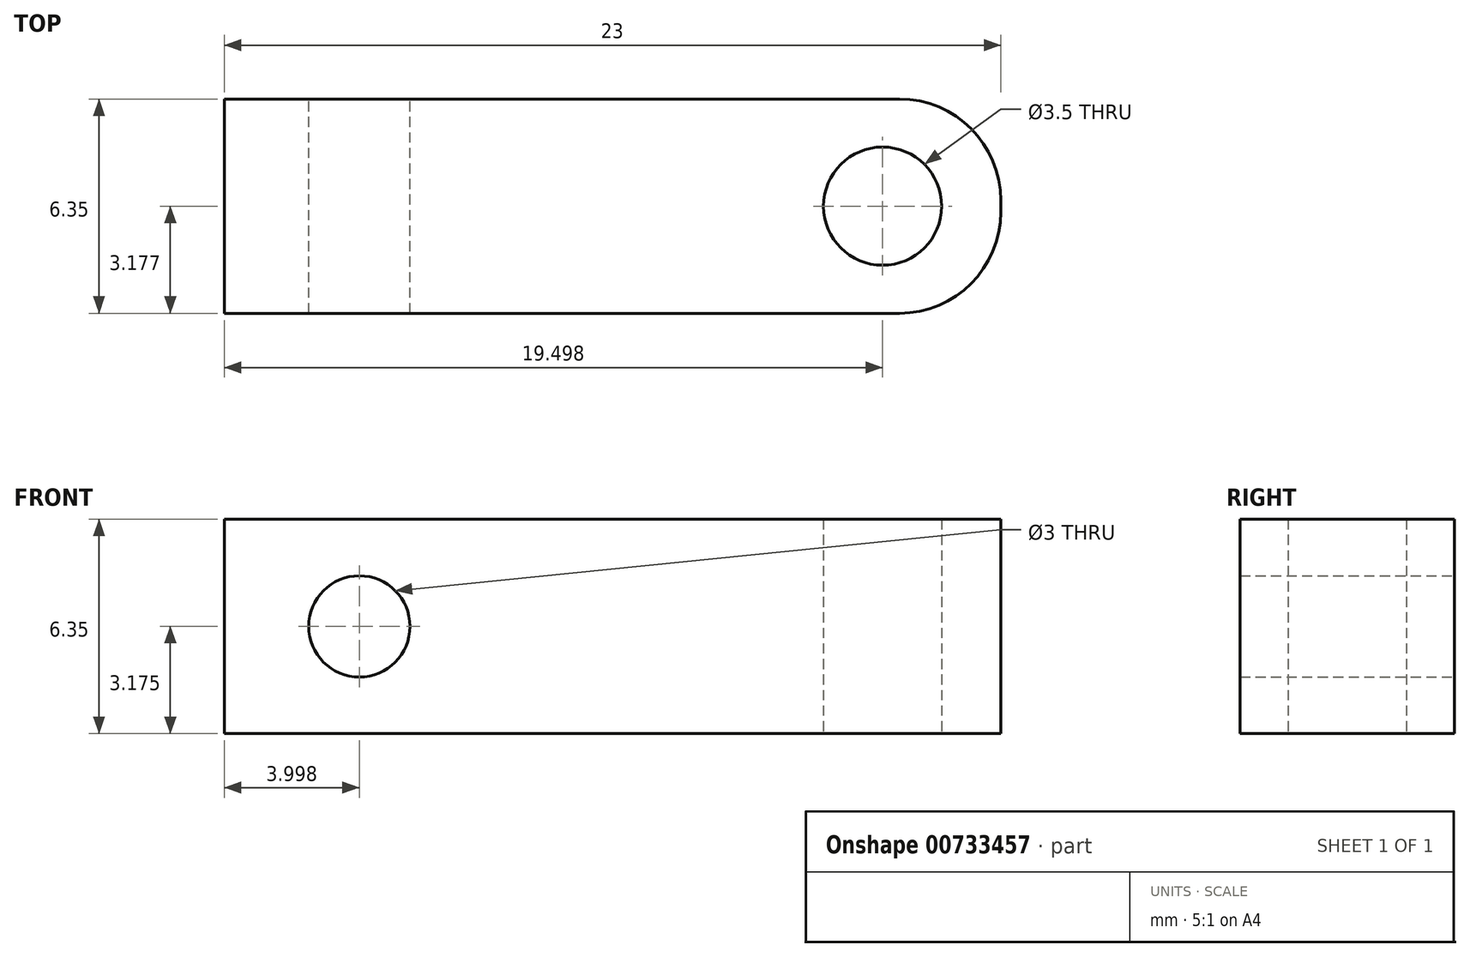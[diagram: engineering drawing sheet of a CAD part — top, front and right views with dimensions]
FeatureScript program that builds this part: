
annotation { "Feature Type Name" : "Feature", "Feature Type Description" : "" }
export const myFeature = defineFeature(function(context is Context, id is Id, definition is map)
    precondition{}
    {
        {
            var Q0;
            Q0=qCreatedBy(makeId("Top.planeOp"),FACE);
            var sketch = newSketch(context, id + "F0", { "sketchPlane" : qUnion([Q0])});
            skLineSegment(sketch, "E0.bottom", {"start": v(-11.74, 2.98) * mm, "end": v(8.26, 2.98) * mm});
            skLineSegment(sketch, "E0.top", {"start": v(-11.74, -3.37) * mm, "end": v(8.26, -3.37) * mm});
            skLineSegment(sketch, "E0.left", {"start": v(-11.74, 2.98) * mm, "end": v(-11.74, -3.37) * mm});
            skLineSegment(sketch, "E0.right", {"start": v(11.26, -0.02) * mm, "end": v(11.26, -0.37) * mm});
            skLineSegment(sketch, "E1", {"start": v(-11.74, -0.2) * mm, "end": v(11.26, -0.2) * mm});
            skCircle(sketch, "E2", {"center": v(7.76, -0.2) * mm, "radius": 1.75 * mm});
            skPoint(sketch, "E3.visualSharp", {"position": v(11.26, 2.98) * mm});
            skArc(sketch, "E3.filletArc", {"start": v(11.26, -0.02) * mm, "mid": v(10.38, 2.1) * mm, "end": v(8.26, 2.98) * mm});
            skPoint(sketch, "E4.visualSharp", {"position": v(11.26, -3.37) * mm});
            skArc(sketch, "E4.filletArc", {"start": v(8.26, -3.37) * mm, "mid": v(10.38, -2.49) * mm, "end": v(11.26, -0.37) * mm});
            skSolve(sketch);
        }
        {
            var Q0;
            Q0 = qSketchRegion(id + "F0", true);
            extrude(context, id + "F1", {"entities" : qUnion([Q0]), "depth" : 6.35 * mm, "offsetDistance" : 25 * mm});
        }
        {
            var Q0;
            Q0=qCreatedBy(makeId("Front.planeOp"),FACE);
            var sketch = newSketch(context, id + "F2", { "sketchPlane" : qUnion([Q0])});
            skCircle(sketch, "E5", {"center": v(-7.74, 3.17) * mm, "radius": 1.5 * mm});
            skSolve(sketch);
        }
        {
            var Q0;
            Q0 = qSketchRegion(id + "F2", true);
            extrude(context, id + "F3", {"entities" : qUnion([Q0]), "operationType" : NewBodyOperationType.REMOVE, "endBound" : BoundingType.SYMMETRIC, "depth" : 25 * mm, "offsetDistance" : 25 * mm});
        }
    });
